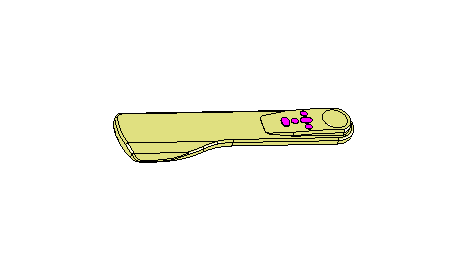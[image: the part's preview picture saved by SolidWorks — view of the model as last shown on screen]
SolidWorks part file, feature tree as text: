
SOLIDWORKS PART (.sldprt)
format: sldprt  version: not decoded by parser v0  size: 1,093,632 bytes
history: native  units: mm
features: sketch x20, cut_extrude x10, plane x8, extrude x7, fillet x2, material x1, boolean_combine x1, chamfer x1, revolve x1, shell x1 + 1 further entry (+7 scaffold rows collapsed)
feature tree (60):
  scaffold x7  (default folders/planes/origin — collapsed)
  material  "Matériau <non spécifié>"
  "Corps de surface"
  plane  "Face"
  plane  "Dessus"
  plane  "Droite"
  sketch  "Contour corps"  dims[D2=76.0mm D1=0.0mm]
  sketch  "Esquisse1"
  plane  "Symetrie verticale"
  plane  "Plan2"  Offset=20mm
  sketch  "Esquisse3"  dims[c1.D3=15.0mm c1.D4=20.0mm c1.D5=140.0mm c1.D6=150.0mm c1.D10=380.0mm c1.D11=~413.139473mm c1.D12=140.0mm c1.D13=380.0mm c2.D10=245.0mm c2.D12=250.0mm c2.D2=79.78mm c2.D7=37.0mm c2.D8=42.0mm c2.D9=285.0mm c2.D11=100.0mm c3.D12=300.0mm c3.D11=160.0mm c4.D12=80.0mm c4.D13=~36.596445mm c4.D1=0.0mm]
  extrude  "Extrusion1"  Depth=33mm
  sketch  "Esquisse4"  dims[D1=20.0mm]
  cut_extrude  "Enlèv. mat.-Extru.4"  Depth=170mm
  sketch  "Esquisse5"  dims[c1.D1=~41.439392mm c2.D1=15.0deg c2.D2=~19.448094mm c3.D2=45.0deg c3.D3=22.0mm c3.D4=50.0mm c3.D5=30.0mm c3.D6=5.0mm]
  cut_extrude  "Enlèv. mat.-Extru.3"  [1 undecoded]
  sketch  "Esquisse6"  dims[c1.D1=~39.892997mm c2.D1=80.0deg c2.D2=26.0mm c2.D3=26.0mm c2.D4=1.0mm c2.D5=60.0mm c2.D6=250.0mm c3.D4=3.0mm]
  extrude  "Extrusion2"  Depth=60mm
  sketch  "Esquisse8"  dims[c1.D1=32.0mm c1.D2=32.0mm c1.D3=32.0mm c1.D4=10.0mm c2.D2=38.0mm c2.D3=140.0mm c2.D4=25.0mm c2.D5=15.0mm c2.D6=15.0mm c2.D7=70.0mm c3.D2=1.0mm]
  extrude  "Extrusion3"  Depth=60mm
  boolean_combine  "Combiner1"
  chamfer  "Chanfrein11"  Distance=7mm Angle=15deg
  fillet  "Congé3"  Radius=4mm
  sketch  "Esquisse11"  dims[D1=52.0mm D2=8.0mm]
  revolve  "Révolution1"  Angle=180deg
  fillet  "Combiner2"  [1 undecoded]
  shell  "Coque1"  Thickness=4.5mm
  sketch  "Esquisse12"  dims[D1=0.0mm]
  cut_extrude  "Enlèv. mat.-Extru.5"  [1 undecoded]
  plane  "Plan3"
  sketch  "Esquisse13"  dims[D1=2.0mm D2=2.0mm]
  extrude  "Extrusion4"  [1 undecoded]
  sketch  "Esquisse17"  dims[D1=1.0mm D2=1.0mm]
  extrude  "Extrusion5"  Depth=5mm
  sketch  "Esquisse18"  dims[c1.D1=17.0mm c1.D2=17.0mm c1.D3=17.0mm c2.D2=6.0mm c2.D3=7.75mm]
  cut_extrude  "Enlèv. mat.-Extru.6"  [1 undecoded]
  sketch  "Esquisse19"  dims[c1.D3=10.0mm c1.D1=15.0mm c1.D2=~31.589725mm c2.D2=100.0deg c2.D3=~31.589725mm c3.D3=100.0deg]
  cut_extrude  "Enlèv. mat.-Extru.7"  [1 undecoded]
  sketch  "Esquisse20"  dims[D1=3.0mm D2=8.0mm D3=8.0mm]
  cut_extrude  "Enlèv. mat.-Extru.8"  [1 undecoded]
  sketch  "Esquisse21"  dims[D1=56.0mm D2=11.0mm D3=7.0mm]
  cut_extrude  "Enlèv. mat.-Extru.9"  [1 undecoded]
  sketch  "Esquisse22"  dims[c1.D5=6.0mm c1.D1=~62.92983mm c2.D1=~0.154402deg c3.D1=7.0mm c3.D2=13.0mm c3.D3=~11.398759mm c4.D3=75.0deg c4.D4=55.0mm]
  cut_extrude  "Enlèv. mat.-Extru.10"  [1 undecoded]
  sketch  "Esquisse23"  dims[D1=1.0mm]
  cut_extrude  "Enlèv. mat.-Extru.11"  [1 undecoded]
  sketch  "Esquisse24"  dims[c1.D1=14.0mm c1.D3=14.0mm c1.D6=39.89mm c1.D2=17.0mm c2.D3=17.0mm c2.D4=22.0mm c2.D5=18.0mm c2.D6=56.0mm c2.D7=12.0mm c2.D8=8.0mm c2.D9=8.0mm c2.D10=12.0mm]
  cut_extrude  "Enlèv. mat.-Extru.13"  [1 undecoded]
  plane  "Plan4"
  plane  "Plan5"  Offset=15mm
  sketch  "Esquisse25"  dims[c1.D1=55.0mm c1.D2=65.0mm c1.D3=10.0mm c1.D4=80.0mm c2.D1=10.0mm]
  extrude  "Extrusion7"  [1 undecoded]
  extrude  "Extrusion9"  [1 undecoded]
  sketch  "Esquisse25<3>"  dims[D1=8.0mm D3=4.0deg]
decode coverage: 28 of 43 modeling features carry decoded parameters; 1 rows unclassified (native names shown)
note: ~ marks probable driven/reference dimensions
note: 13 parameter values undecoded
summary: no parameter record found for 13 features
note: suppression state not decoded; provenance and decode notes live in map.json
